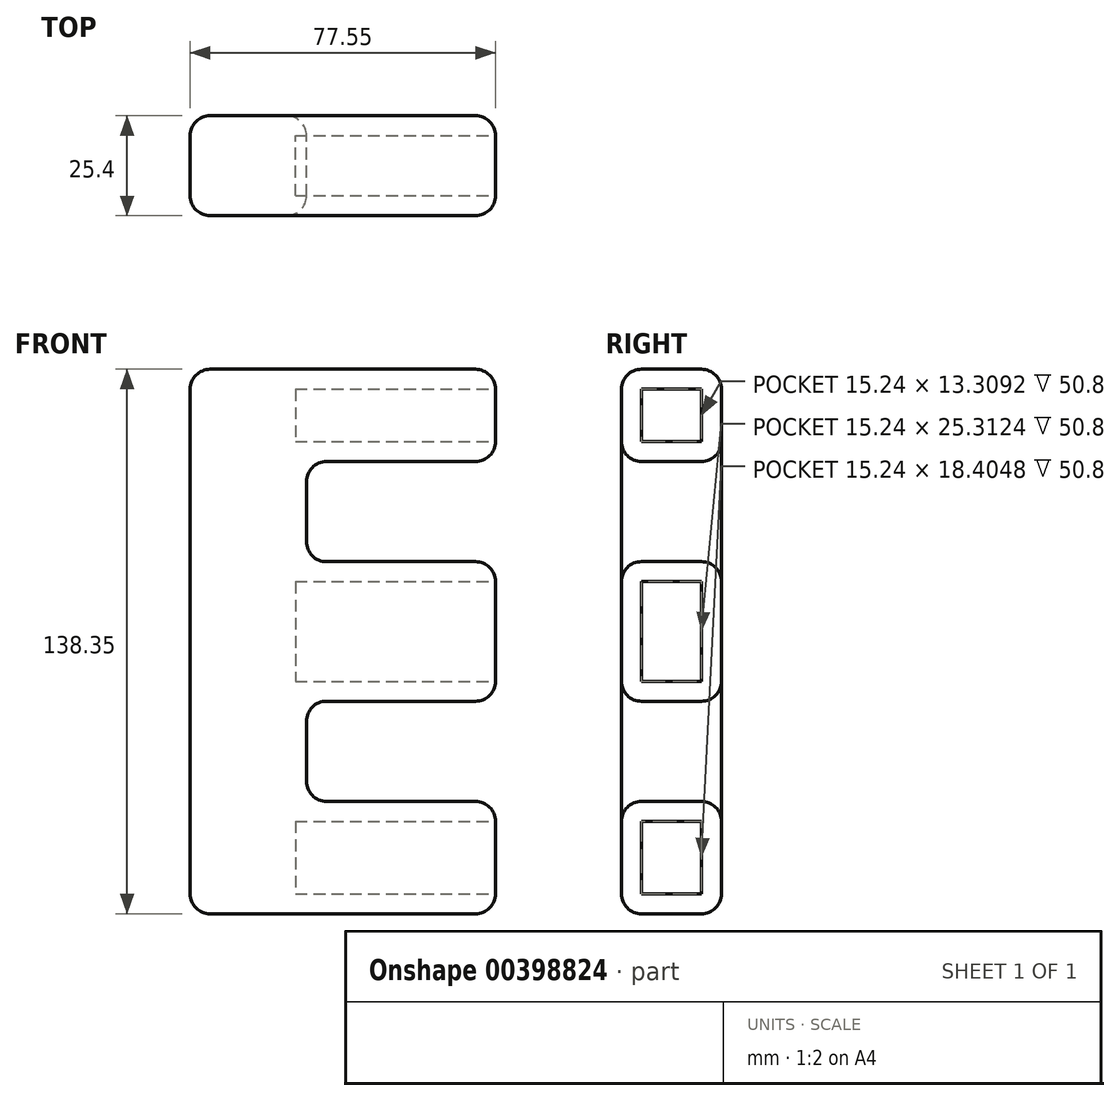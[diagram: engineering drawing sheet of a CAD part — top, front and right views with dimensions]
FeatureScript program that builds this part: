
annotation { "Feature Type Name" : "Feature", "Feature Type Description" : "" }
export const myFeature = defineFeature(function(context is Context, id is Id, definition is map)
    precondition{}
    {
        {
            var Q0;
            Q0=qCreatedBy(makeId("Front.planeOp"),FACE);
            var sketch = newSketch(context, id + "F0", { "sketchPlane" : qUnion([Q0])});
            skLineSegment(sketch, "E0.bottom", {"start": v(-68.03, 69.19) * mm, "end": v(9.52, 69.19) * mm});
            skLineSegment(sketch, "E0.top", {"start": v(-68.03, -69.16) * mm, "end": v(9.52, -69.16) * mm});
            skLineSegment(sketch, "E0.left", {"start": v(-68.03, 69.19) * mm, "end": v(-68.03, -69.16) * mm});
            skLineSegment(sketch, "E0.right", {"start": v(9.52, 69.19) * mm, "end": v(9.52, -69.16) * mm});
            skSolve(sketch);
        }
        {
            var Q0;
            Q0=makeQuery(id+"F0.imprint","IMPRINT",FACE,{"disambiguationData":[TD([[makeQuery(id+"F0.imprint","IMPRINT",EDGE,{"derivedFrom":sQuery(id+"F0.wireOp",EDGE,"E0.bottom")}),-1.0]])]});
            extrude(context, id + "F1", {"entities" : qUnion([Q0]), "depth" : 25.4 * mm});
        }
        {
            var Q0;
            Q0=makeQuery(id+"F1.opExtrude","SWEPT_FACE",FACE,{"disambiguationData":[OSD([sQuery(id+"F0.wireOp",EDGE,"E0.right")])]});
            var sketch = newSketch(context, id + "F2", { "sketchPlane" : qUnion([Q0])});
            skLineSegment(sketch, "E1.bottom", {"start": v(-25.4, 45.72) * mm, "end": v(0, 45.72) * mm});
            skLineSegment(sketch, "E1.top", {"start": v(-25.4, 20.3) * mm, "end": v(0, 20.3) * mm});
            skLineSegment(sketch, "E1.left", {"start": v(-25.4, 45.72) * mm, "end": v(-25.4, 20.3) * mm});
            skLineSegment(sketch, "E1.right", {"start": v(0, 45.72) * mm, "end": v(0, 20.3) * mm});
            skLineSegment(sketch, "E2.bottom", {"start": v(-25.4, -15.17) * mm, "end": v(0, -15.17) * mm});
            skLineSegment(sketch, "E2.top", {"start": v(-25.4, -40.6) * mm, "end": v(0, -40.6) * mm});
            skLineSegment(sketch, "E2.left", {"start": v(-25.4, -15.17) * mm, "end": v(-25.4, -40.6) * mm});
            skLineSegment(sketch, "E2.right", {"start": v(0, -15.17) * mm, "end": v(0, -40.6) * mm});
            skSolve(sketch);
        }
        {
            var Q0;
            Q0 = qSketchRegion(id + "F2", true);
            extrude(context, id + "F3", {"entities" : qUnion([Q0]), "operationType" : NewBodyOperationType.REMOVE, "oppositeDirection" : true, "depth" : 48 * mm});
        }
        {
            var Q0;
            Q0=makeQuery(id+"F1.opExtrude","CAP_FACE",FACE,{"disambiguationData":[OSD([sQuery(id+"F0.wireOp",EDGE,"E0.bottom"),sQuery(id+"F0.wireOp",EDGE,"E0.top"),sQuery(id+"F0.wireOp",EDGE,"E0.left"),sQuery(id+"F0.wireOp",EDGE,"E0.right")])],"isStart":false});
            var Q1;
            Q1=makeQuery(id+"F1.opExtrude","CAP_FACE",FACE,{"disambiguationData":[OSD([sQuery(id+"F0.wireOp",EDGE,"E0.bottom"),sQuery(id+"F0.wireOp",EDGE,"E0.top"),sQuery(id+"F0.wireOp",EDGE,"E0.left"),sQuery(id+"F0.wireOp",EDGE,"E0.right")])],"isStart":true});
            var Q2;
            Q2=makeQuery(id+"F1.opExtrude","SWEPT_FACE",FACE,{"disambiguationData":[OSD([sQuery(id+"F0.wireOp",EDGE,"E0.left")])]});
            var Q3;
            Q3=makeQuery(id+"F1.opExtrude","SWEPT_FACE",FACE,{"disambiguationData":[OSD([sQuery(id+"F0.wireOp",EDGE,"E0.bottom")])]});
            var Q4;
            Q4=makeQuery(id+"F3.boolean.opBoolean","COPY",FACE,{"derivedFrom":makeQuery(id+"F3.opExtrude","SWEPT_FACE",FACE,{"disambiguationData":[OSD([sQuery(id+"F2.wireOp",EDGE,"E1.bottom")])]})});
            var Q5;
            Q5=makeQuery(id+"F3.boolean.opBoolean","COPY",FACE,{"derivedFrom":makeQuery(id+"F3.opExtrude","SWEPT_FACE",FACE,{"disambiguationData":[OSD([sQuery(id+"F2.wireOp",EDGE,"E2.bottom")])]})});
            var Q6;
            Q6=makeQuery(id+"F3.boolean.opBoolean","COPY",FACE,{"derivedFrom":makeQuery(id+"F3.opExtrude","SWEPT_FACE",FACE,{"disambiguationData":[OSD([sQuery(id+"F2.wireOp",EDGE,"E1.top")])]})});
            var Q7;
            Q7=makeQuery(id+"F1.opExtrude","SWEPT_FACE",FACE,{"disambiguationData":[OSD([sQuery(id+"F0.wireOp",EDGE,"E0.top")])]});
            var Q8;
            Q8=makeQuery(id+"F3.boolean.opBoolean","COPY",FACE,{"derivedFrom":makeQuery(id+"F3.opExtrude","SWEPT_FACE",FACE,{"disambiguationData":[OSD([sQuery(id+"F2.wireOp",EDGE,"E2.top")])]})});
            fillet(context, id + "F4", {"entities" : qUnion([Q0, Q1, Q2, Q3, Q4, Q5, Q6, Q7, Q8]), "radius" : 5.08 * mm, "tangentPropagation" : true, "allowEdgeOverflow" : false});
        }
        {
            var Q0;
            {var subQ0=sQuery(id+"F0.wireOp",EDGE,"E0.bottom");var subQ1=sQuery(id+"F0.wireOp",EDGE,"E0.right");Q0=makeQuery(id+"F3.boolean.opBoolean","SPLIT",FACE,{"disambiguationData":[TD([makeQuery(id+"F1.opExtrude","SWEPT_FACE",FACE,{"disambiguationData":[OSD([subQ0])]})])],"derivedFrom":makeQuery(id+"F1.opExtrude","SWEPT_FACE",FACE,{"disambiguationData":[OSD([subQ1])]})});}
            extrude(context, id + "F5", {"entities" : qUnion([Q0]), "operationType" : NewBodyOperationType.REMOVE, "oppositeDirection" : true, "depth" : 50.8 * mm});
        }
        {
            var Q0;
            {var subQ0=sQuery(id+"F0.wireOp",EDGE,"E0.right");Q0=makeQuery(id+"F3.boolean.opBoolean","SPLIT",FACE,{"disambiguationData":[TD([makeQuery(id+"F3.opExtrude","SWEPT_FACE",FACE,{"disambiguationData":[OSD([sQuery(id+"F2.wireOp",EDGE,"E1.top")])]})])],"derivedFrom":makeQuery(id+"F1.opExtrude","SWEPT_FACE",FACE,{"disambiguationData":[OSD([subQ0])]})});}
            extrude(context, id + "F6", {"entities" : qUnion([Q0]), "operationType" : NewBodyOperationType.REMOVE, "oppositeDirection" : true, "depth" : 50.8 * mm});
        }
        {
            var Q0;
            {var subQ0=sQuery(id+"F0.wireOp",EDGE,"E0.right");var subQ2=sQuery(id+"F0.wireOp",EDGE,"E0.top");Q0=makeQuery(id+"F3.boolean.opBoolean","SPLIT",FACE,{"disambiguationData":[TD([makeQuery(id+"F1.opExtrude","SWEPT_FACE",FACE,{"disambiguationData":[OSD([subQ2])]})])],"derivedFrom":makeQuery(id+"F1.opExtrude","SWEPT_FACE",FACE,{"disambiguationData":[OSD([subQ0])]})});}
            extrude(context, id + "F7", {"entities" : qUnion([Q0]), "operationType" : NewBodyOperationType.REMOVE, "oppositeDirection" : true, "depth" : 50.8 * mm});
        }
    });
